# Revit family: Uchiwa
name_source: partatom
category: Furniture
revit_build: Autodesk Revit 2016 (Build: 20161004_0715(x64)
units: mm (PartAtom-declared; Revit-internal decimal feet)

## family parameters
Always vertical = Yes
Cut with Voids When Loaded = No
OmniClass Number = 23.40.20.00
OmniClass Title = General Furniture and Specialties
Room Calculation Point = No
Shared = No
Work Plane-Based = No

## types (1)
- Uchiwa
    Base = HAY Matt laquered Oak Horizontal
    Depth = 86.6cm - 34inch
    Description = Capacious and inviting armchair, taking its soft and open shape from the traditional Japanese hand fan. The soft version is ideal for home use, while the moulded foam version is suitable for more demanding contract contexts.
    Design = Doshi Levien
    Height = 106.2cm - 41.8inch
    Legs = HAY Matt laquered Oak Vertical
    Manufacturer = HAY
    Model = Uchiwa
    Price = Contact HAY or visit hay.dk
    Seat = HAY Hallingdal - 130
    Seat Height = 37.8cm - 14.9inch
    Seat Shell = HAY Hallingdal - 130
    Strength, durability and safety = EN 16139:2013 L2
    Type Comments = Polypropylene shell with moulded polyurethane foam.
    URL = https://hay.dk
    Upholstery fabric = Available in a large selection of standard fabrics and leathers.
    Upholstery type = Full upholstery
    Variations = Variability of textiles, colours and base finishes.
    Width = 87.2cm - 34.3inch

## geometry (parser evidence)
native form markers: Revolve x1, Sweep x2
no freeform markers — native parametric forms only
